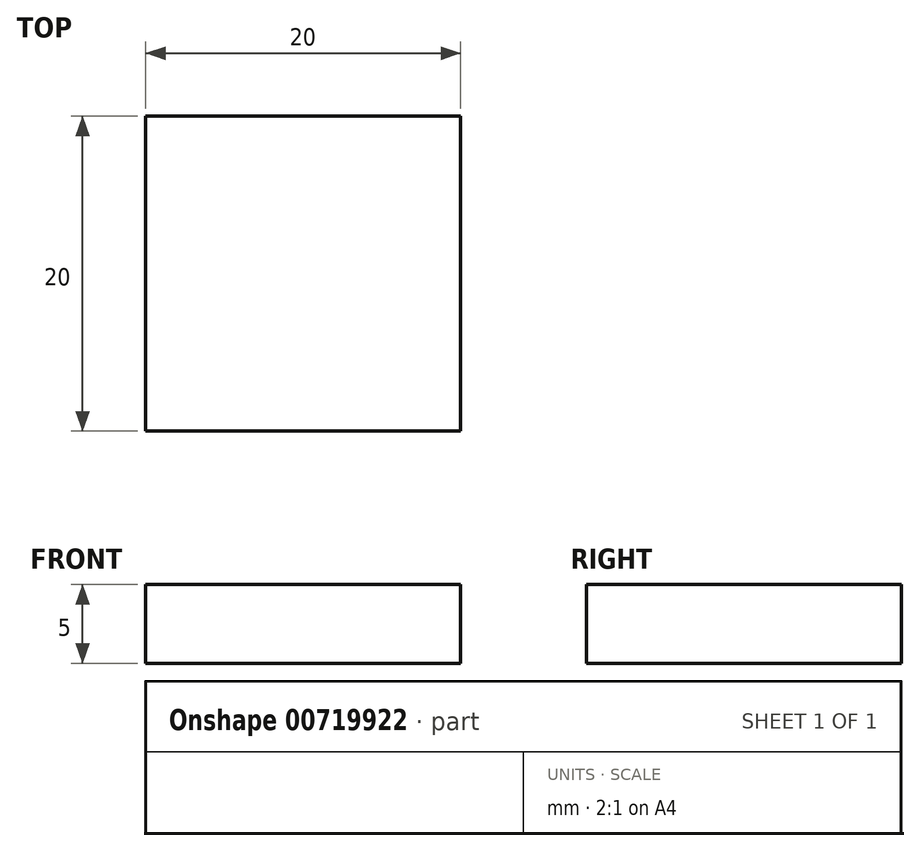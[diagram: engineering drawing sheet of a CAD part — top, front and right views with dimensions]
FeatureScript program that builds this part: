
annotation { "Feature Type Name" : "Feature", "Feature Type Description" : "" }
export const myFeature = defineFeature(function(context is Context, id is Id, definition is map)
    precondition{}
    {
        {
            var Q0;
            Q0=qCreatedBy(makeId("Top.planeOp"),FACE);
            var sketch = newSketch(context, id + "F0", { "sketchPlane" : qUnion([Q0])});
            skLineSegment(sketch, "E0.bottom", {"start": v(0, 0) * mm, "end": v(20, 0) * mm});
            skLineSegment(sketch, "E0.top", {"start": v(0, -20) * mm, "end": v(20, -20) * mm});
            skLineSegment(sketch, "E0.left", {"start": v(0, 0) * mm, "end": v(0, -20) * mm});
            skLineSegment(sketch, "E0.right", {"start": v(20, 0) * mm, "end": v(20, -20) * mm});
            skSolve(sketch);
        }
        {
            var Q0;
            Q0 = qSketchRegion(id + "F0", true);
            extrude(context, id + "F1", {"entities" : qUnion([Q0]), "depth" : 5 * mm, "offsetDistance" : 25 * mm});
        }
    });
